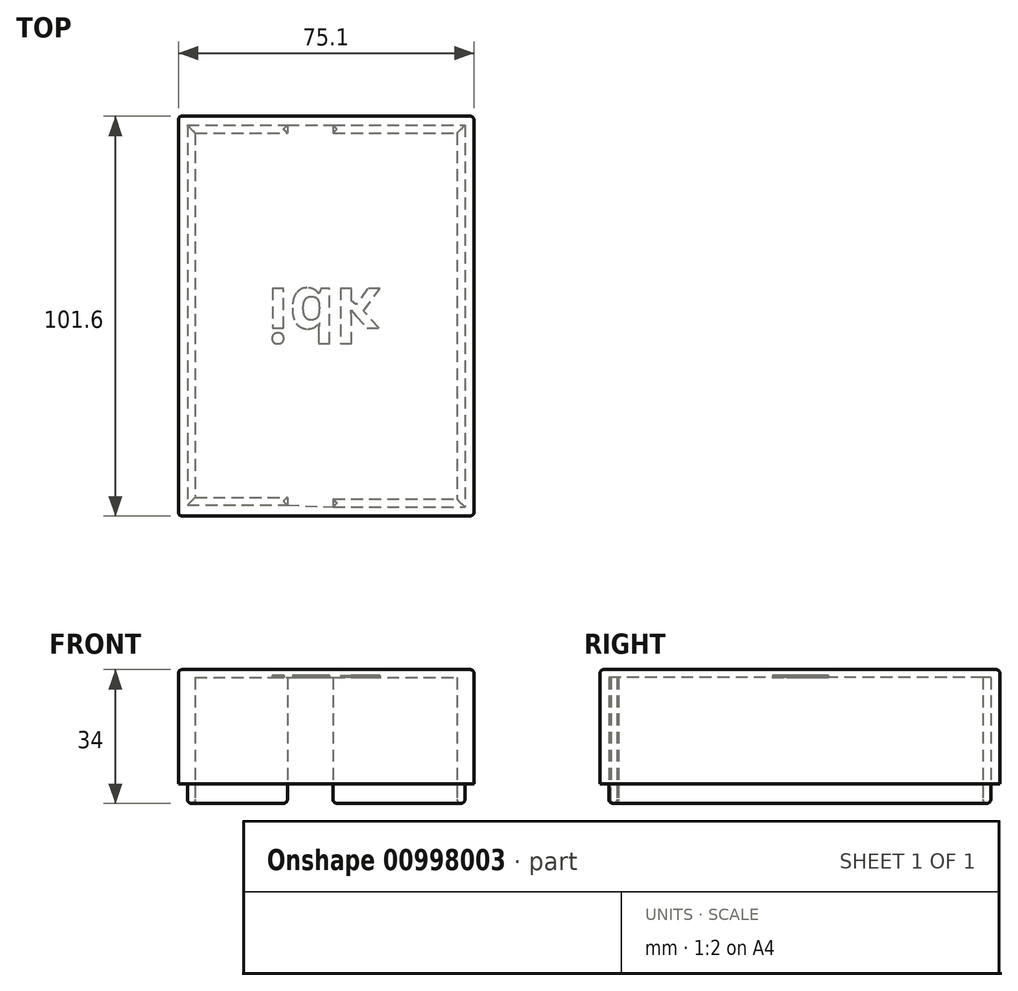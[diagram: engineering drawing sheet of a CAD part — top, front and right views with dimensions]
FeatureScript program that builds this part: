
annotation { "Feature Type Name" : "Feature", "Feature Type Description" : "" }
export const myFeature = defineFeature(function(context is Context, id is Id, definition is map)
    precondition{}
    {
        {
            var Q0;
            Q0=qCreatedBy(makeId("Top.planeOp"),FACE);
            var sketch = newSketch(context, id + "F0", { "sketchPlane" : qUnion([Q0])});
            skLineSegment(sketch, "E0.bottom", {"start": v(0, 50.8) * mm, "end": v(38.1, 50.8) * mm});
            skLineSegment(sketch, "E0.top", {"start": v(0, -50.8) * mm, "end": v(38.1, -50.8) * mm});
            skLineSegment(sketch, "E0.left", {"start": v(0, 50.8) * mm, "end": v(0, -50.8) * mm});
            skLineSegment(sketch, "E0.right", {"start": v(38.1, 50.8) * mm, "end": v(38.1, -50.8) * mm});
            skLineSegment(sketch, "E1.bottom", {"start": v(2.3, 48.5) * mm, "end": v(35.8, 48.5) * mm});
            skLineSegment(sketch, "E1.top", {"start": v(2.3, -48.5) * mm, "end": v(35.8, -48.5) * mm});
            skLineSegment(sketch, "E1.left", {"start": v(2.3, 48.5) * mm, "end": v(2.3, -48.5) * mm});
            skLineSegment(sketch, "E1.right", {"start": v(35.8, 48.5) * mm, "end": v(35.8, -48.5) * mm});
            skLineSegment(sketch, "E2.bottom", {"start": v(0, 50.8) * mm, "end": v(-7, 50.8) * mm});
            skLineSegment(sketch, "E2.top", {"start": v(0, -50.8) * mm, "end": v(-7, -50.8) * mm});
            skLineSegment(sketch, "E2.right", {"start": v(-7, 50.8) * mm, "end": v(-7, -50.8) * mm});
            skLineSegment(sketch, "E3.bottom", {"start": v(-7, 50.8) * mm, "end": v(-37, 50.8) * mm});
            skLineSegment(sketch, "E3.top", {"start": v(-7, -50.8) * mm, "end": v(-37, -50.8) * mm});
            skLineSegment(sketch, "E3.right", {"start": v(-37, 50.8) * mm, "end": v(-37, -50.8) * mm});
            skLineSegment(sketch, "E4.bottom", {"start": v(-34.7, 48.5) * mm, "end": v(-9.3, 48.5) * mm});
            skLineSegment(sketch, "E4.top", {"start": v(-34.7, -48.04) * mm, "end": v(-9.3, -48.04) * mm});
            skLineSegment(sketch, "E4.left", {"start": v(-34.7, 48.5) * mm, "end": v(-34.7, -48.04) * mm});
            skLineSegment(sketch, "E4.right", {"start": v(-9.3, 48.5) * mm, "end": v(-9.3, -48.04) * mm});
            skLineSegment(sketch, "E5.bottom", {"start": v(-32.7, 46.5) * mm, "end": v(-9.3, 46.5) * mm});
            skLineSegment(sketch, "E5.top", {"start": v(-32.7, -46.04) * mm, "end": v(-9.3, -46.04) * mm});
            skLineSegment(sketch, "E5.left", {"start": v(-32.7, 46.5) * mm, "end": v(-32.7, -46.04) * mm});
            skLineSegment(sketch, "E5.right", {"start": v(-9.3, 46.5) * mm, "end": v(-9.3, -46.04) * mm});
            skLineSegment(sketch, "E6.bottom", {"start": v(2.3, 46.5) * mm, "end": v(33.8, 46.5) * mm});
            skLineSegment(sketch, "E6.top", {"start": v(2.3, -46.5) * mm, "end": v(33.8, -46.5) * mm});
            skLineSegment(sketch, "E6.left", {"start": v(2.3, 46.5) * mm, "end": v(2.3, -46.5) * mm});
            skLineSegment(sketch, "E6.right", {"start": v(33.8, 46.5) * mm, "end": v(33.8, -46.5) * mm});
            skLineSegment(sketch, "E7", {"start": v(-9.3, 48.5) * mm, "end": v(2.3, 48.5) * mm});
            skLineSegment(sketch, "E8", {"start": v(-9.3, -48.04) * mm, "end": v(2.3, -48.5) * mm});
            skLineSegment(sketch, "E9", {"start": v(-9.3, 46.5) * mm, "end": v(-9.3, 48.5) * mm});
            skLineSegment(sketch, "E10", {"start": v(2.3, 46.5) * mm, "end": v(2.3, 48.5) * mm});
            skLineSegment(sketch, "E11", {"start": v(2.3, -48.5) * mm, "end": v(2.3, -46.5) * mm});
            skLineSegment(sketch, "E12", {"start": v(-9.3, -48.04) * mm, "end": v(-9.3, -46.04) * mm});
            skSolve(sketch);
        }
        {
            var Q0;
            {var subQ1=sQuery(id+"F0.wireOp",EDGE,"E3.bottom");Q0=makeQuery(id+"F0.imprint","IMPRINT",FACE,{"disambiguationData":[TD([[makeQuery(id+"F0.imprint","IMPRINT",EDGE,{"derivedFrom":subQ1}),1.0]])]});}
            var Q1;
            {var subQ0=sQuery(id+"F0.wireOp",EDGE,"E2.bottom");Q1=makeQuery(id+"F0.imprint","IMPRINT",FACE,{"disambiguationData":[TD([[makeQuery(id+"F0.imprint","IMPRINT",EDGE,{"derivedFrom":subQ0}),1.0]])]});}
            var Q2;
            {var subQ1=sQuery(id+"F0.wireOp",EDGE,"E0.bottom");Q2=makeQuery(id+"F0.imprint","IMPRINT",FACE,{"disambiguationData":[TD([[makeQuery(id+"F0.imprint","IMPRINT",EDGE,{"derivedFrom":subQ1}),-1.0]])]});}
            var Q3;
            {var subQ0=sQuery(id+"F0.wireOp",EDGE,"E2.top");Q3=makeQuery(id+"F0.imprint","IMPRINT",FACE,{"disambiguationData":[TD([[makeQuery(id+"F0.imprint","IMPRINT",EDGE,{"derivedFrom":subQ0}),-1.0]])]});}
            var Q4;
            {var subQ3=sQuery(id+"F0.wireOp",EDGE,"E4.bottom");Q4=makeQuery(id+"F0.imprint","IMPRINT",FACE,{"disambiguationData":[TD([[makeQuery(id+"F0.imprint","IMPRINT",EDGE,{"derivedFrom":subQ3}),-1.0]])]});}
            var Q5;
            {var subQ3=sQuery(id+"F0.wireOp",EDGE,"E1.bottom");Q5=makeQuery(id+"F0.imprint","IMPRINT",FACE,{"disambiguationData":[TD([[makeQuery(id+"F0.imprint","IMPRINT",EDGE,{"derivedFrom":subQ3}),-1.0]])]});}
            extrude(context, id + "F1", {"entities" : qUnion([Q0, Q1, Q2, Q3, Q4, Q5]), "depth" : 29 * mm, "offsetDistance" : 25 * mm});
        }
        {
            var Q0;
            {var subQ3=sQuery(id+"F0.wireOp",EDGE,"E4.bottom");Q0=makeQuery(id+"F0.imprint","IMPRINT",FACE,{"disambiguationData":[TD([[makeQuery(id+"F0.imprint","IMPRINT",EDGE,{"derivedFrom":subQ3}),-1.0]])]});}
            var Q1;
            {var subQ3=sQuery(id+"F0.wireOp",EDGE,"E1.bottom");Q1=makeQuery(id+"F0.imprint","IMPRINT",FACE,{"disambiguationData":[TD([[makeQuery(id+"F0.imprint","IMPRINT",EDGE,{"derivedFrom":subQ3}),-1.0]])]});}
            var Q2;
            Q2=sQuery(id+"F0.wireOp",EDGE,"E6.right");
            var Q3;
            Q3=sQuery(id+"F0.wireOp",EDGE,"E6.bottom");
            var Q4;
            Q4=sQuery(id+"F0.wireOp",EDGE,"E1.bottom");
            var Q5;
            Q5=sQuery(id+"F0.wireOp",EDGE,"E1.right");
            var Q6;
            Q6=sQuery(id+"F0.wireOp",EDGE,"E6.top");
            var Q7;
            Q7=sQuery(id+"F0.wireOp",EDGE,"E1.top");
            var Q8;
            Q8=sQuery(id+"F0.wireOp",EDGE,"E5.top");
            var Q9;
            Q9=sQuery(id+"F0.wireOp",EDGE,"E4.top");
            var Q10;
            Q10=sQuery(id+"F0.wireOp",EDGE,"E5.left");
            var Q11;
            Q11=sQuery(id+"F0.wireOp",EDGE,"E4.left");
            var Q12;
            Q12=sQuery(id+"F0.wireOp",EDGE,"E4.bottom");
            var Q13;
            Q13=sQuery(id+"F0.wireOp",EDGE,"E5.bottom");
            var Q14;
            Q14=sQuery(id+"F0.wireOp",EDGE,"E11");
            var Q15;
            Q15=sQuery(id+"F0.wireOp",EDGE,"E12");
            var Q16;
            Q16=sQuery(id+"F0.wireOp",EDGE,"E10");
            extrude(context, id + "F2", {"entities" : qUnion([Q0, Q1]), "operationType" : NewBodyOperationType.ADD, "surfaceEntities" : qUnion([Q2, Q3, Q4, Q5, Q6, Q7, Q8, Q9, Q10, Q11, Q12, Q13, Q14, Q15, Q16]), "oppositeDirection" : true, "depth" : 5 * mm, "offsetDistance" : 25 * mm});
        }
        {
            var Q0;
            Q0=makeQuery(id+"F1.opExtrude","CAP_FACE",FACE,{"disambiguationData":[OSD([sQuery(id+"F0.wireOp",EDGE,"E0.bottom"),sQuery(id+"F0.wireOp",EDGE,"E0.top"),sQuery(id+"F0.wireOp",EDGE,"E0.right"),sQuery(id+"F0.wireOp",EDGE,"E1.left"),sQuery(id+"F0.wireOp",EDGE,"E2.bottom"),sQuery(id+"F0.wireOp",EDGE,"E2.top"),sQuery(id+"F0.wireOp",EDGE,"E3.bottom"),sQuery(id+"F0.wireOp",EDGE,"E3.top"),sQuery(id+"F0.wireOp",EDGE,"E3.right"),sQuery(id+"F0.wireOp",EDGE,"E4.right"),sQuery(id+"F0.wireOp",EDGE,"E5.bottom"),sQuery(id+"F0.wireOp",EDGE,"E5.top"),sQuery(id+"F0.wireOp",EDGE,"E5.left"),sQuery(id+"F0.wireOp",EDGE,"E6.bottom"),sQuery(id+"F0.wireOp",EDGE,"E6.top"),sQuery(id+"F0.wireOp",EDGE,"E6.right"),sQuery(id+"F0.wireOp",EDGE,"E7"),sQuery(id+"F0.wireOp",EDGE,"E8")])],"isStart":false});
            var sketch = newSketch(context, id + "F3", { "sketchPlane" : qUnion([Q0])});
            skSolve(sketch);
        }
        {
            var Q0;
            {var subQ3=sQuery(id+"F0.wireOp",EDGE,"E5.bottom");Q0=makeQuery(id+"F3.imprint","IMPRINT",FACE,{"disambiguationData":[TD([[makeQuery(id+"F3.imprint","IMPRINT",EDGE,{"derivedFrom":makeQuery(id+"F1.opExtrude","CAP_EDGE",EDGE,{"disambiguationData":[OSD([subQ3])],"isStart":false})}),-1.0]])]});}
            extrude(context, id + "F4", {"entities" : qUnion([Q0]), "operationType" : NewBodyOperationType.ADD, "oppositeDirection" : true, "depth" : 2 * mm, "offsetDistance" : 25 * mm});
        }
        {
            var Q0;
            Q0=makeQuery(id+"F2.opExtrude","CAP_EDGE",EDGE,{"disambiguationData":[OSD([sQuery(id+"F0.wireOp",EDGE,"E6.bottom")])],"isStart":false});
            var Q1;
            Q1=makeQuery(id+"F2.opExtrude","CAP_EDGE",EDGE,{"disambiguationData":[OSD([sQuery(id+"F0.wireOp",EDGE,"E1.bottom")])],"isStart":false});
            var Q2;
            Q2=makeQuery(id+"F2.opExtrude","CAP_EDGE",EDGE,{"disambiguationData":[OSD([sQuery(id+"F0.wireOp",EDGE,"E1.right")])],"isStart":false});
            var Q3;
            Q3=makeQuery(id+"F2.opExtrude","CAP_EDGE",EDGE,{"disambiguationData":[OSD([sQuery(id+"F0.wireOp",EDGE,"E6.right")])],"isStart":false});
            var Q4;
            Q4=makeQuery(id+"F2.opExtrude","CAP_EDGE",EDGE,{"disambiguationData":[OSD([sQuery(id+"F0.wireOp",EDGE,"E6.top")])],"isStart":false});
            var Q5;
            Q5=makeQuery(id+"F2.opExtrude","CAP_EDGE",EDGE,{"disambiguationData":[OSD([sQuery(id+"F0.wireOp",EDGE,"E1.top")])],"isStart":false});
            var Q6;
            Q6=makeQuery(id+"F2.opExtrude","CAP_EDGE",EDGE,{"disambiguationData":[OSD([sQuery(id+"F0.wireOp",EDGE,"E5.top")])],"isStart":false});
            var Q7;
            Q7=makeQuery(id+"F2.opExtrude","CAP_EDGE",EDGE,{"disambiguationData":[OSD([sQuery(id+"F0.wireOp",EDGE,"E4.top")])],"isStart":false});
            var Q8;
            Q8=makeQuery(id+"F2.opExtrude","CAP_EDGE",EDGE,{"disambiguationData":[OSD([sQuery(id+"F0.wireOp",EDGE,"E5.left")])],"isStart":false});
            var Q9;
            Q9=makeQuery(id+"F2.opExtrude","CAP_EDGE",EDGE,{"disambiguationData":[OSD([sQuery(id+"F0.wireOp",EDGE,"E4.left")])],"isStart":false});
            var Q10;
            Q10=makeQuery(id+"F2.opExtrude","CAP_EDGE",EDGE,{"disambiguationData":[OSD([sQuery(id+"F0.wireOp",EDGE,"E5.bottom")])],"isStart":false});
            var Q11;
            Q11=makeQuery(id+"F2.opExtrude","CAP_EDGE",EDGE,{"disambiguationData":[OSD([sQuery(id+"F0.wireOp",EDGE,"E4.bottom")])],"isStart":false});
            var Q12;
            {var subQ0=sQuery(id+"F0.wireOp",EDGE,"E4.right");Q12=makeQuery(id+"F2.opExtrude","CAP_EDGE",EDGE,{"disambiguationData":[OSD([subQ0]),TDD([makeQuery(id+"F0.imprint","IMPRINT",EDGE,{"disambiguationData":[TD([[makeQuery(id+"F0.imprint","INTERSECT",VERTEX,{"derivedFrom":[subQ0,sQuery(id+"F0.wireOp",EDGE,"E5.bottom")]}),1.0]])],"derivedFrom":subQ0})])],"isStart":false});}
            var Q13;
            {var subQ0=sQuery(id+"F0.wireOp",EDGE,"E1.left");Q13=makeQuery(id+"F2.opExtrude","CAP_EDGE",EDGE,{"disambiguationData":[OSD([subQ0]),TDD([makeQuery(id+"F0.imprint","IMPRINT",EDGE,{"disambiguationData":[TD([[makeQuery(id+"F0.imprint","INTERSECT",VERTEX,{"derivedFrom":[subQ0,sQuery(id+"F0.wireOp",EDGE,"E6.bottom")]}),1.0]])],"derivedFrom":subQ0})])],"isStart":false});}
            var Q14;
            {var subQ0=sQuery(id+"F0.wireOp",EDGE,"E1.left");Q14=makeQuery(id+"F2.opExtrude","CAP_EDGE",EDGE,{"disambiguationData":[OSD([subQ0]),TDD([makeQuery(id+"F0.imprint","IMPRINT",EDGE,{"disambiguationData":[TD([[makeQuery(id+"F0.imprint","INTERSECT",VERTEX,{"derivedFrom":[subQ0,sQuery(id+"F0.wireOp",EDGE,"E6.top")]}),-1.0]])],"derivedFrom":subQ0})])],"isStart":false});}
            var Q15;
            {var subQ0=sQuery(id+"F0.wireOp",EDGE,"E4.right");Q15=makeQuery(id+"F2.opExtrude","CAP_EDGE",EDGE,{"disambiguationData":[OSD([subQ0]),TDD([makeQuery(id+"F0.imprint","IMPRINT",EDGE,{"disambiguationData":[TD([[makeQuery(id+"F0.imprint","INTERSECT",VERTEX,{"derivedFrom":[subQ0,sQuery(id+"F0.wireOp",EDGE,"E5.top")]}),-1.0]])],"derivedFrom":subQ0})])],"isStart":false});}
            var Q16;
            Q16=makeQuery(id+"F1.opExtrude","CAP_EDGE",EDGE,{"disambiguationData":[OSD([sQuery(id+"F0.wireOp",EDGE,"E0.bottom"),sQuery(id+"F0.wireOp",EDGE,"E2.bottom"),sQuery(id+"F0.wireOp",EDGE,"E3.bottom")])],"isStart":false});
            var Q17;
            Q17=makeQuery(id+"F1.opExtrude","CAP_EDGE",EDGE,{"disambiguationData":[OSD([sQuery(id+"F0.wireOp",EDGE,"E0.right")])],"isStart":false});
            var Q18;
            Q18=makeQuery(id+"F1.opExtrude","CAP_EDGE",EDGE,{"disambiguationData":[OSD([sQuery(id+"F0.wireOp",EDGE,"E0.top"),sQuery(id+"F0.wireOp",EDGE,"E2.top"),sQuery(id+"F0.wireOp",EDGE,"E3.top")])],"isStart":false});
            var Q19;
            Q19=makeQuery(id+"F1.opExtrude","CAP_EDGE",EDGE,{"disambiguationData":[OSD([sQuery(id+"F0.wireOp",EDGE,"E3.right")])],"isStart":false});
            var Q20;
            Q20=makeQuery(id+"F1.opExtrude","SWEPT_EDGE",EDGE,{"disambiguationData":[OSD([sQuery(id+"F0.wireOp",EDGE,"E3.top"),sQuery(id+"F0.wireOp",EDGE,"E3.right")])]});
            var Q21;
            Q21=makeQuery(id+"F1.opExtrude","SWEPT_EDGE",EDGE,{"disambiguationData":[OSD([sQuery(id+"F0.wireOp",EDGE,"E3.bottom"),sQuery(id+"F0.wireOp",EDGE,"E3.right")])]});
            var Q22;
            Q22=makeQuery(id+"F1.opExtrude","SWEPT_EDGE",EDGE,{"disambiguationData":[OSD([sQuery(id+"F0.wireOp",EDGE,"E0.bottom"),sQuery(id+"F0.wireOp",EDGE,"E0.right")])]});
            var Q23;
            Q23=makeQuery(id+"F1.opExtrude","SWEPT_EDGE",EDGE,{"disambiguationData":[OSD([sQuery(id+"F0.wireOp",EDGE,"E0.top"),sQuery(id+"F0.wireOp",EDGE,"E0.right")])]});
            fillet(context, id + "F5", {"entities" : qUnion([Q0, Q1, Q2, Q3, Q4, Q5, Q6, Q7, Q8, Q9, Q10, Q11, Q12, Q13, Q14, Q15, Q16, Q17, Q18, Q19, Q20, Q21, Q22, Q23]), "radius" : 1 * mm, "tangentPropagation" : true, "allowEdgeOverflow" : false});
        }
        {
            var Q0;
            Q0=makeQuery(id+"F4.opExtrude","CAP_FACE",FACE,{"disambiguationData":[OSD([sQuery(id+"F0.wireOp",EDGE,"E1.left"),sQuery(id+"F0.wireOp",EDGE,"E4.right"),sQuery(id+"F0.wireOp",EDGE,"E5.bottom"),sQuery(id+"F0.wireOp",EDGE,"E5.top"),sQuery(id+"F0.wireOp",EDGE,"E5.left"),sQuery(id+"F0.wireOp",EDGE,"E6.bottom"),sQuery(id+"F0.wireOp",EDGE,"E6.top"),sQuery(id+"F0.wireOp",EDGE,"E6.right"),sQuery(id+"F0.wireOp",EDGE,"E7"),sQuery(id+"F0.wireOp",EDGE,"E8")])],"isStart":false});
            var sketch = newSketch(context, id + "F6", { "sketchPlane" : qUnion([Q0])});
            skText(sketch, "E13", { "text": "idk", "fontName": "OpenSans-Bold.ttf"});
            const initialGuessF6  = {"E13": [-0.01452, -0.00702, 1, 0, 0.0133]};
            skSetInitialGuess(sketch, initialGuessF6);
            skSolve(sketch);
        }
        {
            var Q0;
            Q0 = qSketchRegion(id + "F6", true);
            extrude(context, id + "F7", {"entities" : qUnion([Q0]), "operationType" : NewBodyOperationType.REMOVE, "oppositeDirection" : true, "depth" : .5 * mm, "offsetDistance" : 25 * mm});
        }
    });
